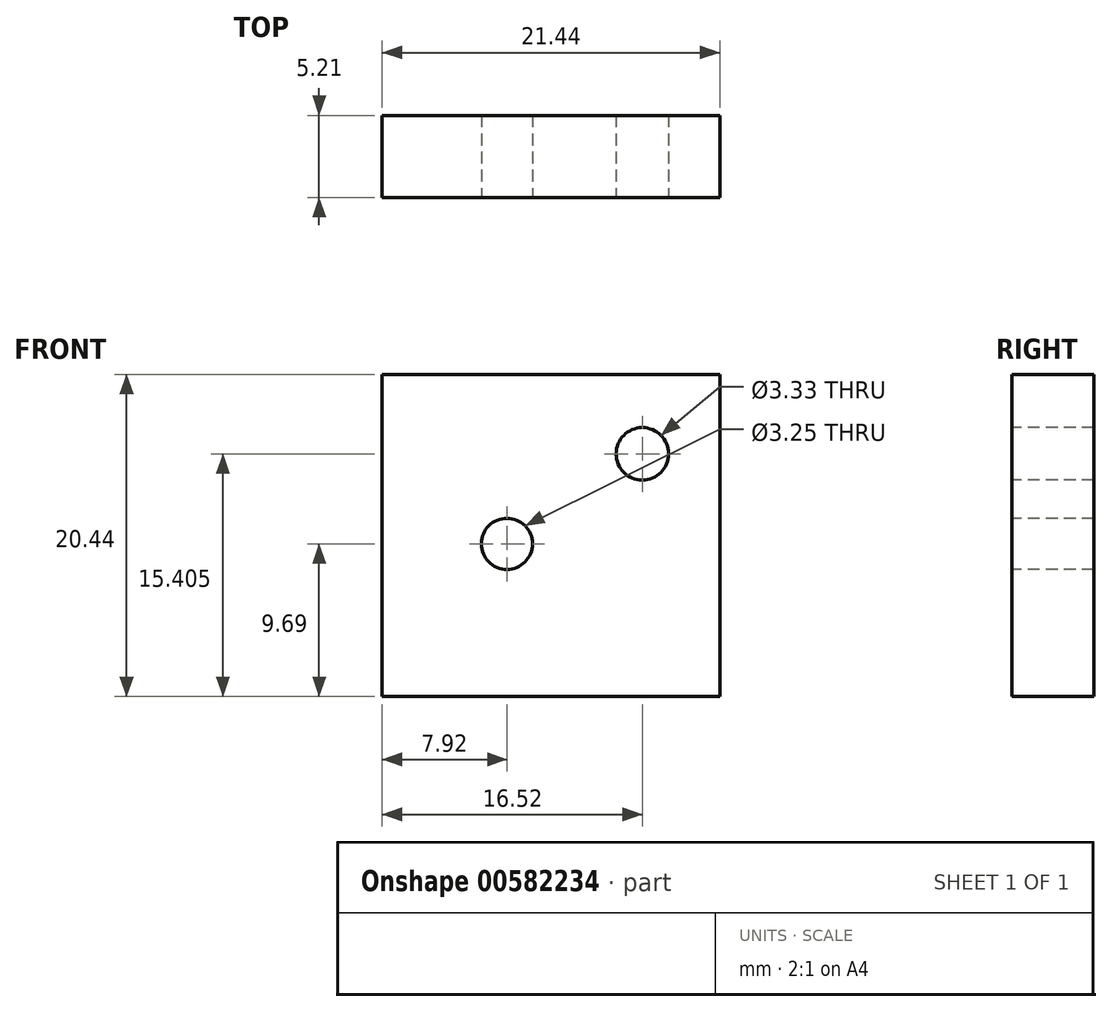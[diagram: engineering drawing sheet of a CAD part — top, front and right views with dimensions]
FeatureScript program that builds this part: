
annotation { "Feature Type Name" : "Feature", "Feature Type Description" : "" }
export const myFeature = defineFeature(function(context is Context, id is Id, definition is map)
    precondition{}
    {
        {
            var Q0;
            Q0=qCreatedBy(makeId("Front.planeOp"),FACE);
            var sketch = newSketch(context, id + "F0", { "sketchPlane" : qUnion([Q0])});
            skLineSegment(sketch, "E0.bottom", {"start": v(-10.72, 10.22) * mm, "end": v(10.73, 10.22) * mm});
            skLineSegment(sketch, "E0.top", {"start": v(-10.73, -10.22) * mm, "end": v(10.72, -10.22) * mm});
            skLineSegment(sketch, "E0.left", {"start": v(-10.72, 10.22) * mm, "end": v(-10.73, -10.22) * mm});
            skLineSegment(sketch, "E0.right", {"start": v(10.73, 10.22) * mm, "end": v(10.72, -10.22) * mm});
            skPoint(sketch, "E0.middle", {"position": v(0, 0) * mm});
            skSolve(sketch);
        }
        {
            var Q0;
            Q0 = qSketchRegion(id + "F0", true);
            extrude(context, id + "F1", {"entities" : qUnion([Q0]), "depth" : 5.2 * mm, "offsetDistance" : 25 * mm});
        }
        {
            var Q0;
            Q0=makeQuery(id+"F1.opExtrude","CAP_FACE",FACE,{"disambiguationData":[OSD([sQuery(id+"F0.wireOp",EDGE,"E0.bottom"),sQuery(id+"F0.wireOp",EDGE,"E0.top"),sQuery(id+"F0.wireOp",EDGE,"E0.left"),sQuery(id+"F0.wireOp",EDGE,"E0.right")])],"isStart":false});
            var sketch = newSketch(context, id + "F2", { "sketchPlane" : qUnion([Q0])});
            skCircle(sketch, "E1", {"center": v(5.8, 5.18) * mm, "radius": 1.67 * mm});
            skSolve(sketch);
        }
        {
            var Q0;
            Q0=makeQuery(id+"F2.imprint","IMPRINT",FACE,{"disambiguationData":[TD([[makeQuery(id+"F2.imprint","IMPRINT",EDGE,{"derivedFrom":sQuery(id+"F2.wireOp",EDGE,"E1")}),-1.0]])]});
            var sketch = newSketch(context, id + "F3", { "sketchPlane" : qUnion([Q0])});
            skCircle(sketch, "E2", {"center": v(-2.8, -0.53) * mm, "radius": 1.63 * mm});
            skSolve(sketch);
        }
        {
            var Q0;
            Q0 = qSketchRegion(id + "F3", true);
            var Q1;
            Q1=makeQuery(id+"F2.imprint","IMPRINT",FACE,{"disambiguationData":[TD([[makeQuery(id+"F2.imprint","IMPRINT",EDGE,{"derivedFrom":sQuery(id+"F2.wireOp",EDGE,"E1")}),1.0]])]});
            extrude(context, id + "F4", {"entities" : qUnion([Q0, Q1]), "operationType" : NewBodyOperationType.REMOVE, "endBound" : BoundingType.THROUGH_ALL, "oppositeDirection" : true, "depth" : 25 * mm, "offsetDistance" : 25 * mm});
        }
    });
